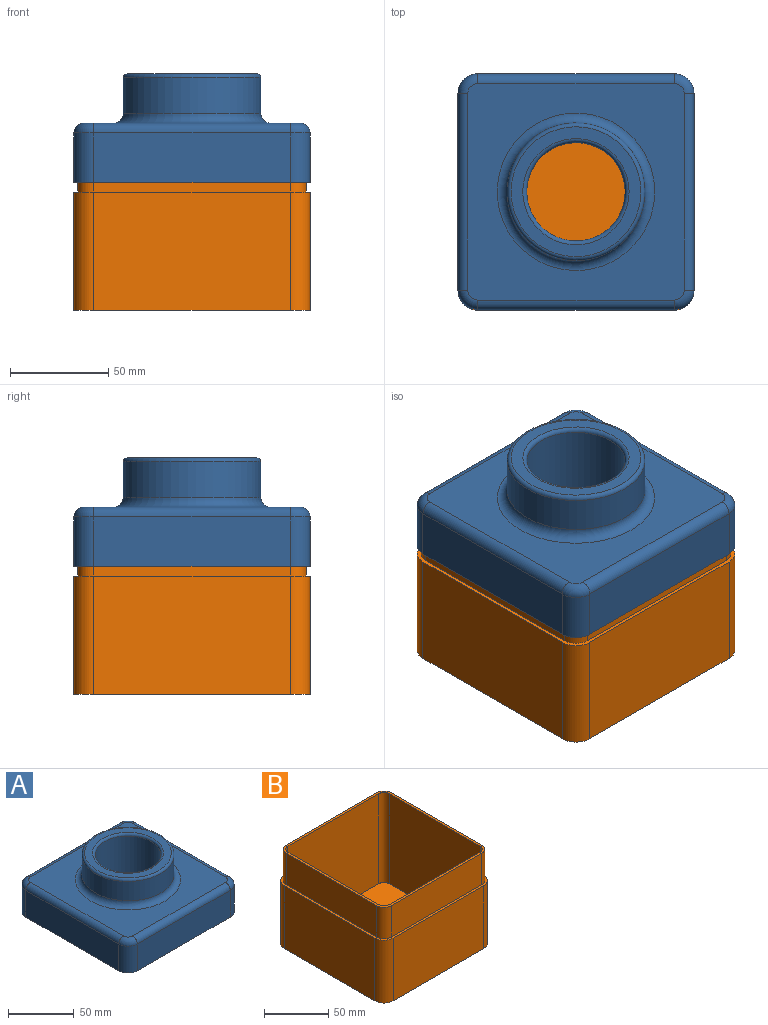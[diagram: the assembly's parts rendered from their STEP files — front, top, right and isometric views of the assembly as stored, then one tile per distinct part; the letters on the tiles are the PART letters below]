
ASSEMBLY  parts=2 mates=1
PART A: 46 faces, bbox 121.6x121.6x55 mm
  f0: plane 54x54mm, normal (0,0,-1), area 326.7mm2, adj f9,f32
  f1: plane 110x110mm, normal (0,0,1), area 7052mm2, adj f12,f13,f14,f15,f16,f18,f20,f22
  f2: plane 100x25mm, normal (0,-1,0), area 2500mm2, adj f6,f13,f21,f23
  f3: plane 100x25mm, normal (1,0,0), area 2500mm2, adj f6,f14,f19,f21
  f4: plane 100x25mm, normal (0,1,0), area 2500mm2, adj f6,f16,f17,f19
  f5: plane 100x25mm, normal (-1,0,0), area 2500mm2, adj f6,f15,f17,f23
  f6: plane 120x120mm, normal (0,0,-1), area 913.1mm2, adj f2,f3,f4,f5,f17,f19,f21,f23
  f7: cylinder r=35mm len=70mm, axis (0,0,-1), area 3958.4mm2, adj f11,f12
  f8: plane 66x66mm, normal (0,0,1), area 1131mm2, adj f10,f11
  f9: cylinder r=25mm len=53mm, axis (0,0,1), area 8325.2mm2, adj f0,f10
  f10: torus R=27mm, axis (0,0,1), area 507.8mm2, adj f8,f9
  f11: torus R=33mm, axis (0,0,1), area 676.5mm2, adj f7,f8
  f12: torus R=40mm, axis (0,0,1), area 1816.8mm2, adj f1,f7
  f13: cylinder r=5mm len=100mm, axis (-1,0,0), area 785.4mm2, adj f1,f2,f22,f24
  f14: cylinder r=5mm len=100mm, axis (0,-1,0), area 785.4mm2, adj f1,f3,f20,f22
  f15: cylinder r=5mm len=100mm, axis (0,1,0), area 785.4mm2, adj f1,f5,f18,f24
  f16: cylinder r=5mm len=100mm, axis (1,0,0), area 785.4mm2, adj f1,f4,f18,f20
  f17: cylinder r=10mm len=25mm, axis (0,0,1), area 392.7mm2, adj f4,f5,f6,f18
  f18: torus R=5mm, axis (0,0,1), area 101mm2, adj f1,f15,f16,f17
  f19: cylinder r=10mm len=25mm, axis (0,0,-1), area 392.7mm2, adj f3,f4,f6,f20
  f20: torus R=5mm, axis (0,0,1), area 101mm2, adj f1,f14,f16,f19
  f21: cylinder r=10mm len=25mm, axis (0,0,1), area 392.7mm2, adj f2,f3,f6,f22
  f22: torus R=5mm, axis (0,0,1), area 101mm2, adj f1,f13,f14,f21
  f23: cylinder r=10mm len=25mm, axis (0,0,-1), area 392.7mm2, adj f2,f5,f6,f24
  f24: torus R=5mm, axis (0,0,1), area 101mm2, adj f1,f13,f15,f23
  f25: plane 110x110mm, normal (0,0,-1), area 7052mm2, adj f33,f34,f35,f36,f37,f39,f41,f43
  f26: plane 100x25mm, normal (0,1,0), area 2500mm2, adj f6,f34,f42,f44
  f27: plane 100x25mm, normal (-1,0,0), area 2500mm2, adj f6,f35,f40,f42
  f28: plane 100x25mm, normal (0,-1,0), area 2500mm2, adj f6,f37,f38,f40
  f29: plane 100x25mm, normal (1,0,0), area 2500mm2, adj f6,f36,f38,f44
  f30: cylinder r=33mm len=66mm, axis (0,0,-1), area 3732.2mm2, adj f31,f33
  f31: plane 66x66mm, normal (0,0,-1), area 1131mm2, adj f30,f32
  f32: cylinder r=27mm len=54mm, axis (0,0,1), area 8991.2mm2, adj f0,f31
  f33: torus R=40mm, axis (0,0,1), area 2455.6mm2, adj f25,f30
  f34: cylinder r=3mm len=100mm, axis (-1,0,0), area 471.2mm2, adj f25,f26,f43,f45
  f35: cylinder r=3mm len=100mm, axis (0,-1,0), area 471.2mm2, adj f25,f27,f41,f43
  f36: cylinder r=3mm len=100mm, axis (0,1,0), area 471.2mm2, adj f25,f29,f39,f45
  f37: cylinder r=3mm len=100mm, axis (1,0,0), area 471.2mm2, adj f25,f28,f39,f41
  f38: cylinder r=8mm len=25mm, axis (0,0,1), area 314.2mm2, adj f6,f28,f29,f39
  f39: torus R=5mm, axis (0,0,1), area 51.1mm2, adj f25,f36,f37,f38
  f40: cylinder r=8mm len=25mm, axis (0,0,-1), area 314.2mm2, adj f6,f27,f28,f41
  f41: torus R=5mm, axis (0,0,1), area 51.1mm2, adj f25,f35,f37,f40
  f42: cylinder r=8mm len=25mm, axis (0,0,1), area 314.2mm2, adj f6,f26,f27,f43
  f43: torus R=5mm, axis (0,0,1), area 51.1mm2, adj f25,f34,f35,f42
  f44: cylinder r=8mm len=25mm, axis (0,0,-1), area 314.2mm2, adj f6,f26,f29,f45
  f45: torus R=5mm, axis (0,0,1), area 51.1mm2, adj f25,f34,f36,f44
PART B: 28 faces, bbox 120x120x90 mm
  f0: plane 116x116mm, normal (0,0,1), area 888mm2, adj f1,f2,f3,f4,f6,f7,f8,f9
  f1: plane 100x86mm, normal (0,1,0), area 8600mm2, adj f0,f5,f6,f9
  f2: plane 100x86mm, normal (-1,0,0), area 8600mm2, adj f0,f5,f6,f7
  f3: plane 100x86mm, normal (0,-1,0), area 8600mm2, adj f0,f5,f7,f8
  f4: plane 100x86mm, normal (1,0,0), area 8600mm2, adj f0,f5,f8,f9
  f5: plane 112x112mm, normal (0,0,1), area 12513.1mm2, adj f1,f2,f3,f4,f6,f7,f8,f9
  f6: cylinder r=6mm len=86mm, axis (0,0,1), area 810.5mm2, adj f0,f1,f2,f5
  f7: cylinder r=6mm len=86mm, axis (0,0,-1), area 810.5mm2, adj f0,f2,f3,f5
  f8: cylinder r=6mm len=86mm, axis (0,0,1), area 810.5mm2, adj f0,f3,f4,f5
  f9: cylinder r=6mm len=86mm, axis (0,0,-1), area 810.5mm2, adj f0,f1,f4,f5
  f10: plane 100x30mm, normal (0,1,0), area 3000mm2, adj f0,f11,f17,f18
  f11: cylinder r=8mm len=30mm, axis (0,0,1), area 377mm2, adj f0,f10,f12,f18
  f12: plane 100x30mm, normal (1,0,0), area 3000mm2, adj f0,f11,f13,f18
  f13: cylinder r=8mm len=30mm, axis (0,0,1), area 377mm2, adj f0,f12,f14,f18
  f14: plane 100x30mm, normal (0,-1,0), area 3000mm2, adj f0,f13,f15,f18
  f15: cylinder r=8mm len=30mm, axis (0,0,1), area 377mm2, adj f0,f14,f16,f18
  f16: plane 100x30mm, normal (-1,0,0), area 3000mm2, adj f0,f15,f17,f18
  f17: cylinder r=8mm len=30mm, axis (0,0,1), area 377mm2, adj f0,f10,f16,f18
  f18: plane 120x120mm, normal (0,0,1), area 913.1mm2, adj f10,f11,f12,f13,f14,f15,f16,f17
  f19: plane 120x120mm, normal (0,0,-1), area 14314.2mm2, adj f20,f21,f22,f23,f24,f25,f26,f27
  f20: cylinder r=10mm len=60mm, axis (0,0,1), area 942.5mm2, adj f18,f19,f22,f24
  f21: cylinder r=10mm len=60mm, axis (0,0,-1), area 942.5mm2, adj f18,f19,f22,f27
  f22: plane 100x60mm, normal (-1,0,0), area 6000mm2, adj f18,f19,f20,f21
  f23: cylinder r=10mm len=60mm, axis (0,0,-1), area 942.5mm2, adj f18,f19,f24,f26
  f24: plane 100x60mm, normal (0,1,0), area 6000mm2, adj f18,f19,f20,f23
  f25: cylinder r=10mm len=60mm, axis (0,0,1), area 942.5mm2, adj f18,f19,f26,f27
  f26: plane 100x60mm, normal (1,0,0), area 6000mm2, adj f18,f19,f23,f25
  f27: plane 100x60mm, normal (0,-1,0), area 6000mm2, adj f18,f19,f21,f25
PLACE A t=(0,0,61)mm
PLACE B t=(0,0,-4)mm
MATE fastened B.f18 <-> A.f9  axis (0,0,1) through (0,0,56)mm
